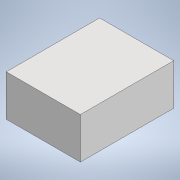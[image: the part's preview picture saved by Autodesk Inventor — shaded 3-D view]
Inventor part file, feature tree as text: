
AUTODESK INVENTOR PART (.ipt)
format: ipt  version: 2022.3 (Build 263350000, 350)  size: 86,528 bytes
history: native  units: mm
features: extrude x1, sketch x1
ambient origin geometry x8: Origin, YZ Plane, XZ Plane, XY Plane, X Axis, Y Axis, Z Axis, Center Point
bodies: Solid1 (feature_tree)
feature tree (2):
  extrude  "Extrusion1"  Depth=3.4mm
  sketch  "Sketch1"  dims[d0=2.7mm d1=3.4mm d2=1.5mm d3=0.0mm]
